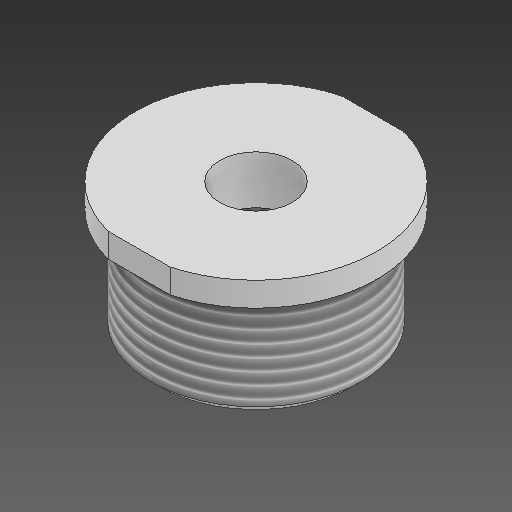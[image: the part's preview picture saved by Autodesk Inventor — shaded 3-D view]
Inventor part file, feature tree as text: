
AUTODESK INVENTOR PART (.ipt)
format: ipt  version: 2021 (Build 250183000, 183)  size: 148,992 bytes
history: native  units: in
note: dims shown in document units (in); Inventor stores cm internally (conversion verified against a paired STEP export)
features: other x3, sketch x2
ambient origin geometry x8: Origin, YZ Plane, XZ Plane, XY Plane, X Axis, Y Axis, Z Axis, Center Point
bodies: Solid1 (feature_tree)
feature tree (5):
  other  "endcap.ipt"
  other  "Solid1::endcap.ipt"
  other  "TaggingFeature1"
  sketch  "Sketch1"  dims[d0=0.3937in]
  sketch  "Sketch2"
